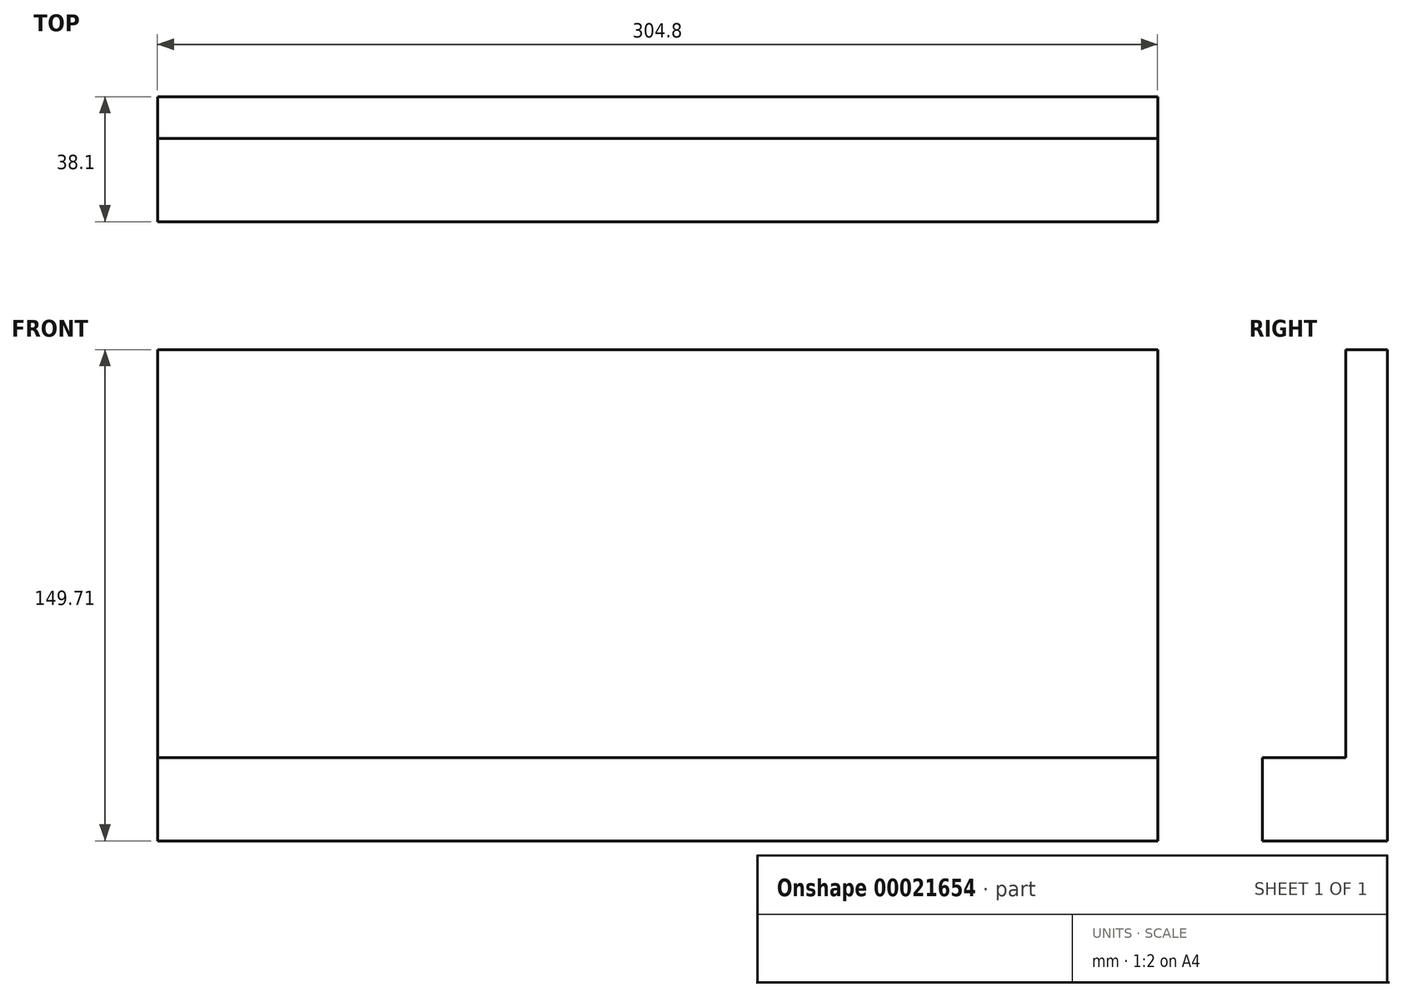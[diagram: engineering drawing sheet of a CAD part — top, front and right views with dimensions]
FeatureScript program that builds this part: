
annotation { "Feature Type Name" : "Feature", "Feature Type Description" : "" }
export const myFeature = defineFeature(function(context is Context, id is Id, definition is map)
    precondition{}
    {
        {
            var Q0;
            Q0=qCreatedBy(makeId("Front.planeOp"),FACE);
            var sketch = newSketch(context, id + "F0", { "sketchPlane" : qUnion([Q0])});
            skLineSegment(sketch, "E0.bottom", {"start": v(-149.05, 82.57) * mm, "end": v(155.75, 82.57) * mm});
            skLineSegment(sketch, "E0.top", {"start": v(-149.05, -67.14) * mm, "end": v(155.75, -67.14) * mm});
            skLineSegment(sketch, "E0.left", {"start": v(-149.05, 82.57) * mm, "end": v(-149.05, -67.14) * mm});
            skLineSegment(sketch, "E0.right", {"start": v(155.75, 82.57) * mm, "end": v(155.75, -67.14) * mm});
            skSolve(sketch);
        }
        {
            var Q0;
            Q0=makeQuery(id+"F0.imprint","IMPRINT",FACE,{"disambiguationData":[TD([[makeQuery(id+"F0.imprint","IMPRINT",EDGE,{"derivedFrom":sQuery(id+"F0.wireOp",EDGE,"E0.bottom")}),-1.0]])]});
            extrude(context, id + "F1", {"entities" : qUnion([Q0]), "depth" : 12.7 * mm});
        }
        {
            var Q0;
            Q0=makeQuery(id+"F1.opExtrude","CAP_FACE",FACE,{"disambiguationData":[OSD([sQuery(id+"F0.wireOp",EDGE,"E0.bottom"),sQuery(id+"F0.wireOp",EDGE,"E0.top"),sQuery(id+"F0.wireOp",EDGE,"E0.left"),sQuery(id+"F0.wireOp",EDGE,"E0.right")])],"isStart":false});
            var sketch = newSketch(context, id + "F2", { "sketchPlane" : qUnion([Q0])});
            skLineSegment(sketch, "E1.bottom", {"start": v(-149.05, -67.14) * mm, "end": v(155.75, -67.14) * mm});
            skLineSegment(sketch, "E1.top", {"start": v(-149.05, -41.74) * mm, "end": v(155.75, -41.74) * mm});
            skLineSegment(sketch, "E1.left", {"start": v(-149.05, -67.14) * mm, "end": v(-149.05, -41.74) * mm});
            skLineSegment(sketch, "E1.right", {"start": v(155.75, -67.14) * mm, "end": v(155.75, -41.74) * mm});
            skSolve(sketch);
        }
        {
            var Q0;
            Q0=makeQuery(id+"F2.imprint","IMPRINT",FACE,{"disambiguationData":[TD([[makeQuery(id+"F2.imprint","IMPRINT",EDGE,{"derivedFrom":sQuery(id+"F2.wireOp",EDGE,"E1.bottom")}),1.0]])]});
            extrude(context, id + "F3", {"entities" : qUnion([Q0]), "operationType" : NewBodyOperationType.ADD, "depth" : 25.4 * mm});
        }
    });
